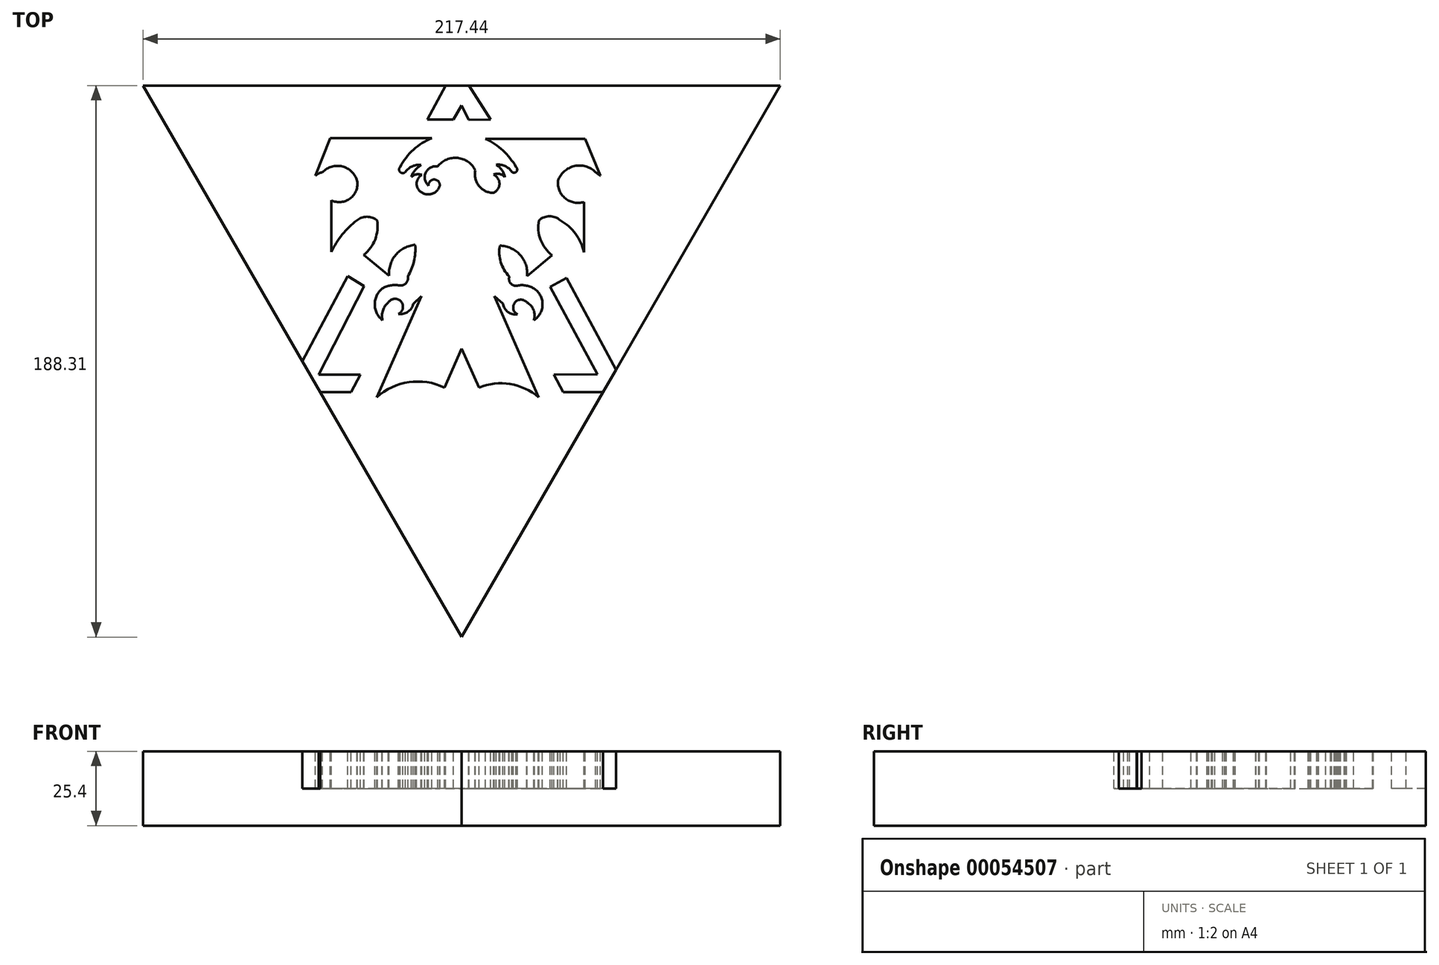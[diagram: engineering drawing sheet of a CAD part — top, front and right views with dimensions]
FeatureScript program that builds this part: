
annotation { "Feature Type Name" : "Feature", "Feature Type Description" : "" }
export const myFeature = defineFeature(function(context is Context, id is Id, definition is map)
    precondition{}
    {
        {
            var Q0;
            Q0=qCreatedBy(makeId("Top.planeOp"),FACE);
            var sketch = newSketch(context, id + "F0", { "sketchPlane" : qUnion([Q0])});
            skCircle(sketch, "E0.cCircle", {"center": v(0, 0) * mm, "radius": 62.77 * mm, "construction": true});
            skLineSegment(sketch, "E0.0", {"start": v(-108.72, 62.77) * mm, "end": v(108.72, 62.77) * mm});
            skLineSegment(sketch, "E0.1", {"start": v(108.72, 62.77) * mm, "end": v(0, -125.54) * mm});
            skLineSegment(sketch, "E0.2", {"start": v(0, -125.54) * mm, "end": v(-108.72, 62.77) * mm});
            skPoint(sketch, "E0.0.midPoint", {"position": v(0, 62.77) * mm});
            skSolve(sketch);
        }
        {
            var Q0;
            Q0=makeQuery(id+"F0.imprint","IMPRINT",FACE,{"disambiguationData":[TD([[makeQuery(id+"F0.imprint","IMPRINT",EDGE,{"derivedFrom":sQuery(id+"F0.wireOp",EDGE,"E0.0")}),-1.0]])]});
            extrude(context, id + "F1", {"entities" : qUnion([Q0]), "depth" : 25.4 * mm});
        }
        {
            var Q0;
            Q0=makeQuery(id+"F1.opExtrude","CAP_FACE",FACE,{"disambiguationData":[OSD([sQuery(id+"F0.wireOp",EDGE,"E0.0"),sQuery(id+"F0.wireOp",EDGE,"E0.1"),sQuery(id+"F0.wireOp",EDGE,"E0.2")])],"isStart":false});
            var sketch = newSketch(context, id + "F2", { "sketchPlane" : qUnion([Q0])});
            skPoint(sketch, "E1", {"position": v(-54.36, -31.38) * mm});
            skPoint(sketch, "E2", {"position": v(-48.26, -41.95) * mm});
            skPoint(sketch, "E3", {"position": v(48.26, -41.95) * mm});
            skPoint(sketch, "E4", {"position": v(52.7, -34.25) * mm});
            skPoint(sketch, "E5", {"position": v(2.49, 62.77) * mm});
            skPoint(sketch, "E6", {"position": v(-5.47, 62.77) * mm});
            skPoint(sketch, "E7", {"position": v(9.91, 51.12) * mm});
            skPoint(sketch, "E8", {"position": v(2.36, 51.04) * mm});
            skPoint(sketch, "E9", {"position": v(0, 56) * mm});
            skPoint(sketch, "E10", {"position": v(-2.84, 51.12) * mm});
            skPoint(sketch, "E11", {"position": v(-11.73, 51.12) * mm});
            skPoint(sketch, "E12", {"position": v(-48.85, -35.95) * mm});
            skPoint(sketch, "E13", {"position": v(-34.56, -35.95) * mm});
            skPoint(sketch, "E14", {"position": v(-37.7, -41.95) * mm});
            skPoint(sketch, "E15", {"position": v(-33.27, -5.73) * mm});
            skPoint(sketch, "E16", {"position": v(-38.9, -2.32) * mm});
            skLineSegment(sketch, "E17", {"start": v(-54.36, -31.38) * mm, "end": v(-38.9, -2.32) * mm});
            skLineSegment(sketch, "E18", {"start": v(-33.27, -5.73) * mm, "end": v(-38.9, -2.32) * mm});
            skLineSegment(sketch, "E19", {"start": v(-33.27, -5.73) * mm, "end": v(-48.85, -35.95) * mm});
            skLineSegment(sketch, "E20", {"start": v(-48.26, -41.95) * mm, "end": v(-37.7, -41.95) * mm});
            skLineSegment(sketch, "E21", {"start": v(-48.85, -35.95) * mm, "end": v(-34.56, -35.95) * mm});
            skLineSegment(sketch, "E22", {"start": v(-34.56, -35.95) * mm, "end": v(-37.7, -41.95) * mm});
            skLineSegment(sketch, "E23", {"start": v(-54.36, -31.38) * mm, "end": v(-48.26, -41.95) * mm});
            skLineSegment(sketch, "E24", {"start": v(52.7, -34.25) * mm, "end": v(48.26, -41.95) * mm});
            skPoint(sketch, "E25", {"position": v(31.52, -35.88) * mm});
            skPoint(sketch, "E26", {"position": v(34.68, -41.95) * mm});
            skLineSegment(sketch, "E27", {"start": v(31.52, -35.88) * mm, "end": v(34.68, -41.95) * mm});
            skLineSegment(sketch, "E28", {"start": v(48.26, -41.95) * mm, "end": v(34.68, -41.95) * mm});
            skLineSegment(sketch, "E29", {"start": v(52.7, -34.25) * mm, "end": v(35.78, -2.88) * mm});
            skLineSegment(sketch, "E30", {"start": v(35.78, -2.88) * mm, "end": v(30.16, -5.91) * mm});
            skLineSegment(sketch, "E31", {"start": v(30.16, -5.91) * mm, "end": v(46.28, -35.78) * mm});
            skLineSegment(sketch, "E32", {"start": v(46.28, -35.78) * mm, "end": v(31.52, -35.88) * mm});
            skPoint(sketch, "E33", {"position": v(-29, -43.66) * mm});
            skPoint(sketch, "E34", {"position": v(-5.9, -40.32) * mm});
            skPoint(sketch, "E35", {"position": v(5.9, -40.32) * mm});
            skPoint(sketch, "E36", {"position": v(0, -27.06) * mm});
            skPoint(sketch, "E37", {"position": v(26.3, -43.66) * mm});
            skPoint(sketch, "E38", {"position": v(11.17, -9.18) * mm});
            skPoint(sketch, "E39", {"position": v(-13.68, -9.18) * mm});
            skPoint(sketch, "E40", {"position": v(14.11, -11.74) * mm});
            skPoint(sketch, "E41", {"position": v(19.02, -15.37) * mm});
            skPoint(sketch, "E42", {"position": v(-16.53, -11.84) * mm});
            skPoint(sketch, "E43", {"position": v(-21.54, -15.17) * mm});
            skPoint(sketch, "E44", {"position": v(-24.98, -11.25) * mm});
            skPoint(sketch, "E45", {"position": v(22.27, -11.25) * mm});
            skPoint(sketch, "E46", {"position": v(24.62, -17.34) * mm});
            skPoint(sketch, "E47", {"position": v(-27.04, -17.34) * mm});
            skArc(sketch, "E48", {"start": v(-5.9, -40.32) * mm, "mid": v(-17.95, -38.5) * mm, "end": v(-29, -43.66) * mm});
            skArc(sketch, "E49", {"start": v(26.3, -43.66) * mm, "mid": v(16.56, -39.16) * mm, "end": v(5.9, -40.32) * mm});
            skLineSegment(sketch, "E50", {"start": v(0, -27.06) * mm, "end": v(-5.9, -40.32) * mm});
            skLineSegment(sketch, "E51", {"start": v(5.9, -40.32) * mm, "end": v(0, -27.06) * mm});
            skLineSegment(sketch, "E52", {"start": v(11.17, -9.18) * mm, "end": v(26.3, -43.66) * mm});
            skLineSegment(sketch, "E53", {"start": v(-29, -43.66) * mm, "end": v(-13.68, -9.18) * mm});
            skLineSegment(sketch, "E54", {"start": v(-16.53, -11.84) * mm, "end": v(-13.68, -9.18) * mm});
            skLineSegment(sketch, "E55", {"start": v(14.11, -11.74) * mm, "end": v(11.17, -9.18) * mm});
            skArc(sketch, "E56", {"start": v(-21.54, -15.17) * mm, "mid": v(-18.37, -14.5) * mm, "end": v(-16.53, -11.84) * mm});
            skArc(sketch, "E57", {"start": v(14.11, -11.74) * mm, "mid": v(15.82, -14.57) * mm, "end": v(19.02, -15.37) * mm});
            skArc(sketch, "E58", {"start": v(22.27, -11.25) * mm, "mid": v(18.15, -11.35) * mm, "end": v(19.02, -15.37) * mm});
            skArc(sketch, "E59", {"start": v(-21.54, -15.17) * mm, "mid": v(-20.7, -10.97) * mm, "end": v(-24.98, -11.25) * mm});
            skArc(sketch, "E60", {"start": v(-24.98, -11.25) * mm, "mid": v(-26.86, -14) * mm, "end": v(-27.04, -17.34) * mm});
            skArc(sketch, "E61", {"start": v(24.62, -17.34) * mm, "mid": v(24.56, -13.86) * mm, "end": v(22.27, -11.25) * mm});
            skPoint(sketch, "E62", {"position": v(-27.04, -6.5) * mm});
            skPoint(sketch, "E63", {"position": v(24.62, -6.5) * mm});
            skArc(sketch, "E64", {"start": v(-27.04, -6.5) * mm, "mid": v(-29.66, -11.92) * mm, "end": v(-27.04, -17.34) * mm});
            skArc(sketch, "E65", {"start": v(24.62, -17.34) * mm, "mid": v(27.6, -11.92) * mm, "end": v(24.62, -6.5) * mm});
            skArc(sketch, "E66", {"start": v(24.62, -6.5) * mm, "mid": v(21.75, -5.47) * mm, "end": v(18.7, -5.6) * mm});
            skArc(sketch, "E67", {"start": v(-21.21, -5.5) * mm, "mid": v(-24.22, -5.46) * mm, "end": v(-27.04, -6.5) * mm});
            skArc(sketch, "E68", {"start": v(16.3, -2.42) * mm, "mid": v(16.65, -4.66) * mm, "end": v(18.7, -5.6) * mm});
            skArc(sketch, "E69", {"start": v(-21.21, -5.5) * mm, "mid": v(-18.99, -4.7) * mm, "end": v(-18.36, -2.42) * mm});
            skArc(sketch, "E70", {"start": v(13, 8.1) * mm, "mid": v(13.36, 2.44) * mm, "end": v(16.3, -2.42) * mm});
            skArc(sketch, "E71", {"start": v(22.37, -2.27) * mm, "mid": v(19.94, 4.96) * mm, "end": v(13, 8.1) * mm});
            skArc(sketch, "E72", {"start": v(-18.36, -2.42) * mm, "mid": v(-16.26, 2.78) * mm, "end": v(-15.83, 8.38) * mm});
            skArc(sketch, "E73", {"start": v(-15.83, 8.38) * mm, "mid": v(-22.48, 4.96) * mm, "end": v(-24.74, -2.18) * mm});
            skPoint(sketch, "E74", {"position": v(-33.37, 4.9) * mm});
            skPoint(sketch, "E75", {"position": v(30.9, 4.8) * mm});
            skLineSegment(sketch, "E76", {"start": v(-33.37, 4.9) * mm, "end": v(-24.74, -2.18) * mm});
            skLineSegment(sketch, "E77", {"start": v(22.37, -2.27) * mm, "end": v(30.9, 4.8) * mm});
            skArc(sketch, "E78", {"start": v(-33.37, 4.9) * mm, "mid": v(-29.52, 10.21) * mm, "end": v(-28.87, 16.74) * mm});
            skArc(sketch, "E79", {"start": v(26.41, 16.74) * mm, "mid": v(26.94, 10.12) * mm, "end": v(30.9, 4.8) * mm});
            skArc(sketch, "E80", {"start": v(33.66, 16.74) * mm, "mid": v(30.04, 18.15) * mm, "end": v(26.41, 16.74) * mm});
            skArc(sketch, "E81", {"start": v(-28.87, 16.74) * mm, "mid": v(-32.31, 17.98) * mm, "end": v(-35.75, 16.74) * mm});
            skArc(sketch, "E82", {"start": v(-35.75, 16.74) * mm, "mid": v(-40.76, 11.9) * mm, "end": v(-44.48, 6) * mm});
            skArc(sketch, "E83", {"start": v(41.75, 5.81) * mm, "mid": v(38.9, 12.15) * mm, "end": v(33.66, 16.74) * mm});
            skLineSegment(sketch, "E84", {"start": v(41.75, 5.81) * mm, "end": v(41.75, 23.01) * mm});
            skLineSegment(sketch, "E85", {"start": v(-44.48, 6) * mm, "end": v(-44.48, 23.57) * mm});
            skArc(sketch, "E86", {"start": v(-44.48, 23.57) * mm, "mid": v(-38.03, 24.24) * mm, "end": v(-35.67, 30.27) * mm});
            skArc(sketch, "E87", {"start": v(32.85, 30.27) * mm, "mid": v(35.36, 24.27) * mm, "end": v(41.75, 23.01) * mm});
            skArc(sketch, "E88", {"start": v(-35.67, 30.27) * mm, "mid": v(-40.72, 35.15) * mm, "end": v(-47.48, 33.2) * mm});
            skArc(sketch, "E89", {"start": v(45.73, 33.2) * mm, "mid": v(38.48, 35.28) * mm, "end": v(32.85, 30.27) * mm});
            skArc(sketch, "E90", {"start": v(45.73, 33.2) * mm, "mid": v(46.53, 32.57) * mm, "end": v(47.36, 31.95) * mm});
            skArc(sketch, "E91", {"start": v(-47.48, 33.2) * mm, "mid": v(-48.81, 32.74) * mm, "end": v(-49.99, 31.95) * mm});
            skLineSegment(sketch, "E92", {"start": v(-49.99, 31.95) * mm, "end": v(-44.84, 44.85) * mm});
            skLineSegment(sketch, "E93", {"start": v(-44.84, 44.85) * mm, "end": v(-10.15, 44.85) * mm});
            skLineSegment(sketch, "E94", {"start": v(47.36, 31.95) * mm, "end": v(42.16, 44.62) * mm});
            skLineSegment(sketch, "E95", {"start": v(42.16, 44.62) * mm, "end": v(8.16, 44.62) * mm});
            skArc(sketch, "E96", {"start": v(-10.15, 44.85) * mm, "mid": v(-16.44, 40.88) * mm, "end": v(-20.98, 35) * mm});
            skArc(sketch, "E97", {"start": v(18.56, 35) * mm, "mid": v(14.07, 40.58) * mm, "end": v(8.16, 44.62) * mm});
            skArc(sketch, "E98", {"start": v(-20.98, 35) * mm, "mid": v(-20.93, 33.2) * mm, "end": v(-19.14, 33.33) * mm});
            skArc(sketch, "E99", {"start": v(17.1, 33.33) * mm, "mid": v(18.7, 33.39) * mm, "end": v(18.56, 35) * mm});
            skArc(sketch, "E100", {"start": v(17.1, 33.33) * mm, "mid": v(14.79, 35.3) * mm, "end": v(11.79, 35.71) * mm});
            skArc(sketch, "E101", {"start": v(14.76, 31.49) * mm, "mid": v(13.77, 33.95) * mm, "end": v(11.79, 35.71) * mm});
            skArc(sketch, "E102", {"start": v(14.76, 31.49) * mm, "mid": v(13, 32.6) * mm, "end": v(10.92, 32.35) * mm});
            skArc(sketch, "E103", {"start": v(-13.61, 32.24) * mm, "mid": v(-15.45, 32.43) * mm, "end": v(-17.13, 31.65) * mm});
            skArc(sketch, "E104", {"start": v(-13.83, 35.66) * mm, "mid": v(-15.86, 33.97) * mm, "end": v(-17.13, 31.65) * mm});
            skArc(sketch, "E105", {"start": v(-13.83, 35.66) * mm, "mid": v(-16.81, 35.24) * mm, "end": v(-19.14, 33.33) * mm});
            skArc(sketch, "E106", {"start": v(-13.61, 32.24) * mm, "mid": v(-15.35, 29.24) * mm, "end": v(-13.61, 26.23) * mm});
            skArc(sketch, "E107", {"start": v(10.92, 26.13) * mm, "mid": v(12.9, 29.24) * mm, "end": v(10.92, 32.35) * mm});
            skArc(sketch, "E108", {"start": v(-7.44, 28.62) * mm, "mid": v(-9.36, 30.7) * mm, "end": v(-11.28, 28.62) * mm});
            skArc(sketch, "E109", {"start": v(-13.61, 26.23) * mm, "mid": v(-9.93, 25.88) * mm, "end": v(-7.44, 28.62) * mm});
            skArc(sketch, "E110", {"start": v(4.7, 33.76) * mm, "mid": v(5.97, 28.45) * mm, "end": v(10.92, 26.13) * mm});
            skArc(sketch, "E111", {"start": v(4.7, 33.76) * mm, "mid": v(-1.33, 38.05) * mm, "end": v(-8.14, 35.17) * mm});
            skArc(sketch, "E112", {"start": v(-8.14, 35.17) * mm, "mid": v(-10.5, 34.81) * mm, "end": v(-12.2, 33.17) * mm});
            skArc(sketch, "E113", {"start": v(-12.2, 33.17) * mm, "mid": v(-12.56, 30.73) * mm, "end": v(-11.28, 28.62) * mm});
            skLineSegment(sketch, "E114", {"start": v(-5.47, 62.77) * mm, "end": v(2.49, 62.77) * mm});
            skLineSegment(sketch, "E115", {"start": v(-2.84, 51.12) * mm, "end": v(-11.73, 51.12) * mm});
            skLineSegment(sketch, "E116", {"start": v(2.36, 51.04) * mm, "end": v(9.91, 51.12) * mm});
            skLineSegment(sketch, "E117", {"start": v(2.49, 62.77) * mm, "end": v(9.91, 51.12) * mm});
            skLineSegment(sketch, "E118", {"start": v(-5.47, 62.77) * mm, "end": v(-11.73, 51.12) * mm});
            skLineSegment(sketch, "E119", {"start": v(0, 56) * mm, "end": v(-2.84, 51.12) * mm});
            skLineSegment(sketch, "E120", {"start": v(0, 56) * mm, "end": v(2.36, 51.04) * mm});
            skSolve(sketch);
        }
        {
            var Q0;
            Q0 = qSketchRegion(id + "F2", true);
            extrude(context, id + "F3", {"entities" : qUnion([Q0]), "operationType" : NewBodyOperationType.REMOVE, "oppositeDirection" : true, "depth" : 12.7 * mm});
        }
    });
